# Revit family: IS_iLife_T4873_BIM_NL
name_source: partatom
category: Plumbing Fixtures
units: mm (PartAtom-declared; Revit-internal decimal feet)

## family parameters
Always vertical = No
Cut with Voids When Loaded = No
OmniClass Number = 23.45.05.14.21.11
OmniClass Title = Bath/Shower Units
Part Type = Normal
Room Calculation Point = No
Round Connector Dimension = Use Diameter
Shared = No
Work Plane-Based = No

## types (1)
- T4873EO - I.LIFE  WALK-IN PANEL 1200 BRIGHT SILVER CLEAR
    Accesoires = https://www.idealstandard.nl
    Accessories = https://www.idealstandard.nl
    Afmetingen = 1154 x 16 x 2002 mm
    AfstandsEenheid = millimeter
    Afwerking = Zilver
    AreaUnits = millimetres
    Artikelnummer = T4873EO
    Artikelomschrijving = I.LIFE WALK-IN PANEL 1200 HELDER ZILVER HELDER
    Artikelreferentie = I.LIFE WALK-IN PANEL 1200 HELDER ZILVER HELDER
    AssetType = Fixed
    Auteur = Ideal Standard
    BIMObjectName = IS_IdealStandard_Showerenclosures_i.Life_T4873
    BIMobject category = Shower screens
    BIMobject category code = shower-screens
    BIMobject main category = Sanitary
    BIMobject main category code = sanitary
    BarCode = 8014140489313
    Beschrijvinggarantie = fabrieksgarantie
    BimObjectNaam = IS_IdealStandard_Showerenclosures_i.Life_T4873
    Brand = Ideal Standard
    Brand url = http://www.idealstandard.nl
    Breedte = 1153.9
    BrutoGewicht = 0
    COBIe Type Category = Plumbing Fixtures
    Color = BRIGHT SILVER CLEAR
    ConnectionType = Plumbing
    CurrencyUnit = €
    CurrentRevision = 1
    Date of publishing = 09/12/2021
    Description = I.LIFE  WALK-IN PANEL 1200 BRIGHT SILVER CLEAR
    Diepte = 16 mm
    DurationUnit = years
    DuurEenheid = Jaar
    Edition number = 1
    Eigenschappen = WALK-IN PANEEL 1200 HELDER ZILVER HELDER
    Features = WALK-IN PANEL 1200 BRIGHT SILVER CLEAR
    Finish = BRIGHT SILVER CLEAR
    GTIN code = https://8014140489313
    Garantieonderdelen = 2
    Garantieunits = Jaar
    GemaaktOp = 10/12/2021
    Help = https://www.idealstandard.nl
    Hoogte = 2002
    Hulp = https://www.idealstandard.nl
    IFC Classification = Sanitary Terminal
    IfcExportAs = IfcSanitaryTerminalType
    IfcExportType = SHOWER
    Installatieinstructies = https://www.idealstandard.nl
    Installation instructions = https://www.idealstandard.nl
    InstallationInstructions = https://www.idealstandard.nl
    Kleur = Zilver
    Lengte = 16 mm
    LinearUnits = millimetres
    MainColor = Silver
    MaintenanceInformation = https://www.idealstandard.nl
    Manufacturer = Ideal Standard
    Manufacturer name = Ideal Standard
    ManufacturerURL = https://www.idealstandard.nl
    Masterformat 2014 Code = 10 28 19
    Masterformat 2014 Description = Tub and Shower Enclosures
    Material = Toughened safety glass
    Material main = tempered glass
    Merk = Ideal Standard
    Model = T4873EO
    ModelNumber = T4873EO
    ModelReference = I.LIFE  WALK-IN PANEL 1200 BRIGHT SILVER CLEAR
    Montageinstuctie = https://www.idealstandard.nl
    NBS Reference Code = 45-35-70/332
    NBS Reference Description = Shower enclosures
    Name = Showerenclosures_i.Life_T4873_IdealStandard
    NettWeight = 52
    Nettogewicht = 52
    NominalDepth = 16 mm
    NominalHeight = 2002 mm  [stored 6.56824 ft]
    NominalLength = 16 mm
    NominalWidth = 1154 mm
    Normen = Showerenclosures_i.Life_T4873_IdealStandard
    OmniClass Code = 23-31 17 17
    OmniClass Description = Shower Enclosures
    OppervlakteEenheid = millimetre
    Product Guid = 2095be92-673e-488d-a9f9-fc2d8985d385
    Product SKU = T4873
    Product certification = https://www.idealstandard.nl
    Product data url = https://bimobject.com
    Product family = I.life
    Product group = Shower Enclosures
    Product name = I.LIFE  WALK-IN PANEL 1200
    Product url = https://www.idealstandard.nl
    ProductInformation = https://www.idealstandard.nl
    ProductSoort = Douchwanden
    Productinformatie = https://www.idealstandard.nl
    QR code = http://bimobject.com
    Revisie = 1
    Shape = rectangular
    Size = 1154 x 16 x 2002 mm
    Space = Internal
    SpareParts = https://www.idealstandard.nl
    Technical description = https://www.idealstandard.nl
    Telefoonnummer = 077 355 08 08
    Typeconnectie = loodgieter
    UNSPSC Code = 30181507
    URL = https://www.idealstandard.nl
    Uniclass 1.4 Code = L72142
    Uniclass 1.4 Description = Shower Screens, curtains
    Uniclass 2.0 Code = PR -35-06-79
    Uniclass 2.0 Description = Shower Enclosures
    Uniclass 2015 Code = Pr_40_20_06_79
    Uniclass 2015 Name = Shower enclosures
    Uniclass2015Beschrijving = Shower Enclosures
    Uniclass2015Code = Pr_40_20_06_79
    Uniclass2015Referentie = Pr_40_20_06_79
    Uniclass2015Title = Shower enclosures
    Uniclass2015Version = v1.22
    Urlproducent = https://www.idealstandard.nl
    ValutaEenheid = Euro
    Versie = 1
    Version = 1
    Vervangingskosten = 0
    VolumeUnits = Litres
    Volumeunits = Liter
    Vorm = rechthoekig
    WRASURL = https://www.wrasapprovals.co.uk
    WarrantyDescription = manufacturer warranty
    WarrantyDurationUnit = Years
    Wisselstukken = https://www.idealstandard.nl
    Youtube clip = https://www.youtube.com

note: [stored X ft] marks values corroborated as IEEE doubles in the binary element streams (Revit-internal decimal feet)

## geometry (parser evidence)
native form markers: Sweep x3
no freeform markers — native parametric forms only
